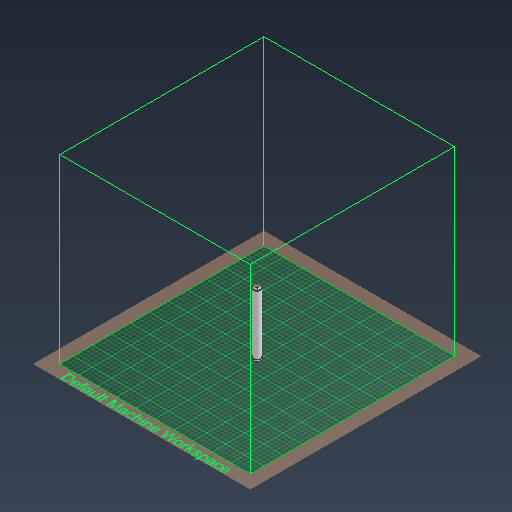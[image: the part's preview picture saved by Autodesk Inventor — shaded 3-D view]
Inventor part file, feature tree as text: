
AUTODESK INVENTOR PART (.ipt)
format: ipt  version: 2021 (Build 250183000, 183)  size: 274,944 bytes
history: native  units: mm
features: extrude x6, sketch x6
ambient origin geometry x8: Origin, YZ Plane, XZ Plane, XY Plane, X Axis, Y Axis, Z Axis, Center Point
bodies: Volumenkörper1 (feature_tree)
feature tree (12):
  extrude  "Extrusion1"  Depth=9.5mm
  extrude  "Extrusion2"  Depth=3.5mm
  extrude  "Extrusion3"  Depth=3.0mm
  extrude  "Extrusion4"  Depth=9.5mm
  extrude  "Extrusion5"  Depth=6.0mm
  extrude  "Extrusion6"  Depth=5.0mm
  sketch  "Skizze1"  dims[d0=9.5mm d1=9.5mm]
  sketch  "Skizze2"  dims[d2=3.5mm d3=0.0mm d4=17.0mm]
  sketch  "Skizze3"  dims[d5=3.0mm d6=0.0mm d7=14.8mm]
  sketch  "Skizze4"  dims[d8=130.0mm d9=0.0mm d10=9.5mm]
  sketch  "Skizze5"  dims[d11=6.0mm d12=0.0mm d13=4.5mm]
  sketch  "Skizze6"  dims[d14=5.0mm d15=0.0mm d16=4.5mm d17=5.0mm d18=0.0mm d19=1.1mm]
